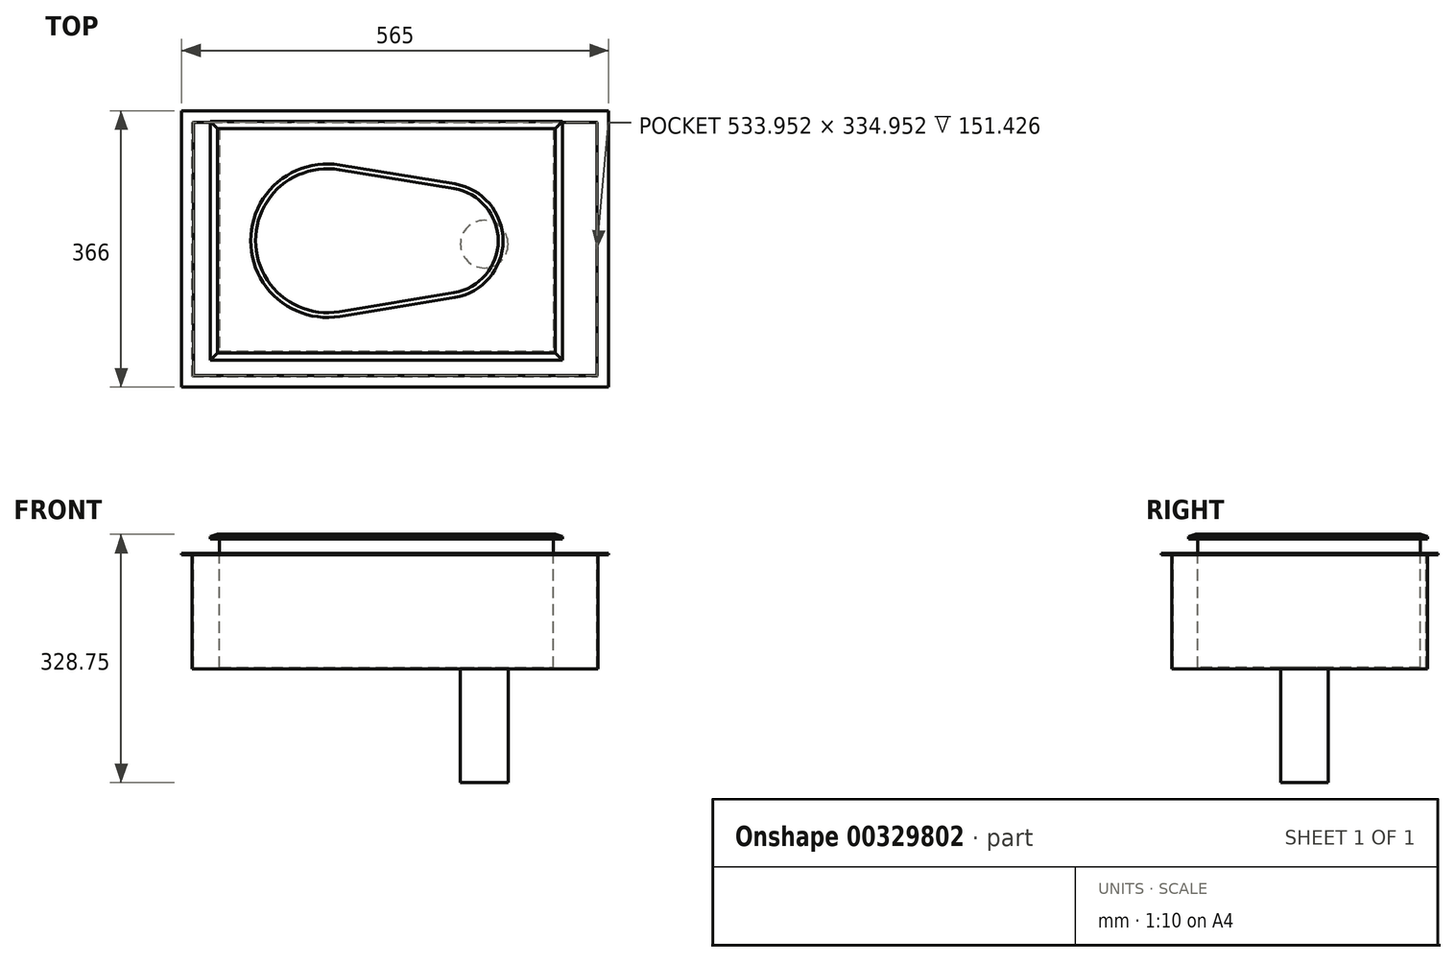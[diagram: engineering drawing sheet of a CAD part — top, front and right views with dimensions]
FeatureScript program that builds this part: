
annotation { "Feature Type Name" : "Feature", "Feature Type Description" : "" }
export const myFeature = defineFeature(function(context is Context, id is Id, definition is map)
    precondition{}
    {
        {
            var Q0;
            Q0=qCreatedBy(makeId("Top.planeOp"),FACE);
            var sketch = newSketch(context, id + "F0", { "sketchPlane" : qUnion([Q0])});
            skLineSegment(sketch, "E0.bottom", {"start": v(0, 0) * mm, "end": v(-466, 0) * mm});
            skLineSegment(sketch, "E0.top", {"start": v(0, 316) * mm, "end": v(-466, 316) * mm});
            skLineSegment(sketch, "E0.left", {"start": v(0, 0) * mm, "end": v(0, 316) * mm});
            skLineSegment(sketch, "E0.right", {"start": v(-466, 0) * mm, "end": v(-466, 316) * mm});
            skSolve(sketch);
        }
        {
            var Q0;
            Q0=qSketchRegion(id+"F0",true);
            extrude(context, id + "F1", {"entities" : qUnion([Q0]), "depth" : 6.35 * mm});
        }
        {
            var Q0;
            Q0=makeQuery(id+"F1.opExtrude","CAP_FACE",FACE,{"disambiguationData":[OSD([sQuery(id+"F0.wireOp",EDGE,"E0.bottom"),sQuery(id+"F0.wireOp",EDGE,"E0.top"),sQuery(id+"F0.wireOp",EDGE,"E0.left"),sQuery(id+"F0.wireOp",EDGE,"E0.right")])],"isStart":false});
            chamfer(context, id + "F2", {"entities" : qUnion([Q0]), "chamferType" : ChamferType.TWO_OFFSETS, "width1" : 3.17 * mm, "oppositeDirection" : false, "width2" : 9.52 * mm, "tangentPropagation" : true});
        }
        {
            var Q0;
            Q0=makeQuery(id+"F1.opExtrude","CAP_FACE",FACE,{"disambiguationData":[OSD([sQuery(id+"F0.wireOp",EDGE,"E0.bottom"),sQuery(id+"F0.wireOp",EDGE,"E0.top"),sQuery(id+"F0.wireOp",EDGE,"E0.left"),sQuery(id+"F0.wireOp",EDGE,"E0.right")])],"isStart":false});
            var sketch = newSketch(context, id + "F3", { "sketchPlane" : qUnion([Q0])});
            skArc(sketch, "E1", {"start": v(-294.53, 258.26) * mm, "mid": v(-412.66, 158.01) * mm, "end": v(-294.53, 57.77) * mm});
            skArc(sketch, "E2", {"start": v(-142.54, 82.83) * mm, "mid": v(-78.74, 158.01) * mm, "end": v(-142.54, 233.2) * mm});
            skLineSegment(sketch, "E3", {"start": v(-294.53, 258.26) * mm, "end": v(-142.54, 233.2) * mm});
            skLineSegment(sketch, "E4", {"start": v(-294.53, 57.77) * mm, "end": v(-142.54, 82.83) * mm});
            skLineSegment(sketch, "E5.0", {"start": v(-295.56, 64.03) * mm, "end": v(-143.58, 89.1) * mm});
            skArc(sketch, "E5.1", {"start": v(-295.56, 252) * mm, "mid": v(-406.3, 158.01) * mm, "end": v(-295.56, 64.03) * mm});
            skLineSegment(sketch, "E5.2", {"start": v(-295.56, 252) * mm, "end": v(-143.58, 226.93) * mm});
            skArc(sketch, "E5.3", {"start": v(-143.58, 89.1) * mm, "mid": v(-85.1, 158.01) * mm, "end": v(-143.58, 226.93) * mm});
            skSolve(sketch);
        }
        {
            var Q0;
            Q0=qSketchRegion(id+"F3",true);
            extrude(context, id + "F4", {"entities" : qUnion([Q0]), "operationType" : NewBodyOperationType.REMOVE, "oppositeDirection" : true, "depth" : 2.54 * mm});
        }
        {
            var Q0;
            Q0=qCreatedBy(makeId("Top.planeOp"),FACE);
            var sketch = newSketch(context, id + "F5", { "sketchPlane" : qUnion([Q0])});
            skLineSegment(sketch, "E6.bottom", {"start": v(-454, 307) * mm, "end": v(-12, 307) * mm});
            skLineSegment(sketch, "E6.top", {"start": v(-454, 12) * mm, "end": v(-12, 12) * mm});
            skLineSegment(sketch, "E6.left", {"start": v(-454, 307) * mm, "end": v(-454, 12) * mm});
            skLineSegment(sketch, "E6.right", {"start": v(-12, 307) * mm, "end": v(-12, 12) * mm});
            skSolve(sketch);
        }
        {
            var Q0;
            Q0=qSketchRegion(id+"F5",true);
            extrude(context, id + "F6", {"entities" : qUnion([Q0]), "operationType" : NewBodyOperationType.ADD, "oppositeDirection" : true, "depth" : 170 * mm});
        }
        {
            var Q0;
            Q0=makeQuery(id+"F6.opExtrude","CAP_FACE",FACE,{"disambiguationData":[OSD([sQuery(id+"F5.wireOp",EDGE,"E6.bottom"),sQuery(id+"F5.wireOp",EDGE,"E6.top"),sQuery(id+"F5.wireOp",EDGE,"E6.left"),sQuery(id+"F5.wireOp",EDGE,"E6.right")])],"isStart":false});
            var sketch = newSketch(context, id + "F7", { "sketchPlane" : qUnion([Q0])});
            skCircle(sketch, "E7", {"center": v(-103.54, -153.5) * mm, "radius": 31.5 * mm});
            skSolve(sketch);
        }
        {
            var Q0;
            Q0=qSketchRegion(id+"F7",true);
            extrude(context, id + "F8", {"entities" : qUnion([Q0]), "operationType" : NewBodyOperationType.ADD, "depth" : 152.4 * mm});
        }
        {
            var Q0;
            Q0=qCreatedBy(makeId("Top.planeOp"),FACE);
            var sketch = newSketch(context, id + "F9", { "sketchPlane" : qUnion([Q0])});
            skLineSegment(sketch, "E8.bottom", {"start": v(-504, -36) * mm, "end": v(61, -36) * mm});
            skLineSegment(sketch, "E8.top", {"start": v(-504, 330) * mm, "end": v(61, 330) * mm});
            skLineSegment(sketch, "E8.left", {"start": v(-504, -36) * mm, "end": v(-504, 330) * mm});
            skLineSegment(sketch, "E8.right", {"start": v(61, -36) * mm, "end": v(61, 330) * mm});
            skLineSegment(sketch, "E9.0", {"start": v(-490, -22) * mm, "end": v(47, -22) * mm});
            skLineSegment(sketch, "E9.1", {"start": v(-490, -22) * mm, "end": v(-490, 316) * mm});
            skLineSegment(sketch, "E9.2", {"start": v(-490, 316) * mm, "end": v(47, 316) * mm});
            skLineSegment(sketch, "E9.3", {"start": v(47, -22) * mm, "end": v(47, 316) * mm});
            skSolve(sketch);
        }
        {
            var Q0;
            Q0=makeQuery(id+"F9.imprint","IMPRINT",FACE,{"disambiguationData":[TD([[makeQuery(id+"F9.imprint","IMPRINT",EDGE,{"derivedFrom":sQuery(id+"F9.wireOp",EDGE,"E9.0")}),1.0]])]});
            extrude(context, id + "F10", {"entities" : qUnion([Q0]), "oppositeDirection" : true, "depth" : 172 * mm, "hasSecondDirection" : true, "secondDirectionOppositeDirection" : true, "secondDirectionDepth" : 19.05 * mm});
        }
        {
            var Q0;
            Q0=makeQuery(id+"F10.opExtrude","CAP_FACE",FACE,{"disambiguationData":[OSD([sQuery(id+"F9.wireOp",EDGE,"E9.0"),sQuery(id+"F9.wireOp",EDGE,"E9.1"),sQuery(id+"F9.wireOp",EDGE,"E9.2"),sQuery(id+"F9.wireOp",EDGE,"E9.3")])],"isStart":true});
            shell(context, id + "F11", {"entities" : qUnion([Q0]), "thickness" : 1.52 * mm});
        }
        {
            var Q0;
            Q0=makeQuery(id+"F9.imprint","IMPRINT",FACE,{"disambiguationData":[TD([[makeQuery(id+"F9.imprint","IMPRINT",EDGE,{"derivedFrom":sQuery(id+"F9.wireOp",EDGE,"E8.bottom")}),1.0]])]});
            extrude(context, id + "F12", {"entities" : qUnion([Q0]), "operationType" : NewBodyOperationType.ADD, "oppositeDirection" : true, "depth" : 20.57 * mm, "hasSecondDirection" : true, "secondDirectionOppositeDirection" : true, "secondDirectionDepth" : 19.05 * mm});
        }
    });
